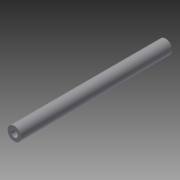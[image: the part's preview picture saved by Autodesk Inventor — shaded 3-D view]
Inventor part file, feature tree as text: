
AUTODESK INVENTOR PART (.ipt)
format: ipt  version: 2015 SP1 (Build 190203100, 203)  size: 71,680 bytes
history: native  units: in
note: dims shown in document units (in); Inventor stores cm internally (conversion verified against a paired STEP export)
features: extrude x1, sketch x1
ambient origin geometry x8: Origin, YZ Plane, XZ Plane, XY Plane, X Axis, Y Axis, Z Axis, Center Point
bodies: Solid1 (feature_tree)
feature tree (2):
  extrude  "Extrusion1"  Depth=1.25in
  sketch  "Sketch1"  dims[d0=2.5in d1=1.25in d2=28.0in d3=0.0in]
